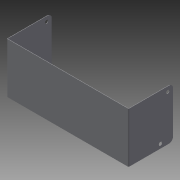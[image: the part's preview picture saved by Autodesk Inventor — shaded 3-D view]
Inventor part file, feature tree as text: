
AUTODESK INVENTOR PART (.ipt)
format: ipt  version: 2014 (Build 180170000, 170)  size: 122,368 bytes
history: native  units: mm
features: sheet_metal_op x4, sketch x3, other x2, chamfer x1, hole x1
ambient origin geometry x8: Origin, YZ Plane, XZ Plane, XY Plane, X Axis, Y Axis, Z Axis, Center Point
bodies: Solid1 (feature_tree)
feature tree (11):
  sheet_metal_op  "Face1"
  sheet_metal_op  "Flange1"
  chamfer  "Corner Round1"
  hole  "Hole1"  [1 undecoded]
  sketch  "Sketch1"  dims[d0=144.0mm d1=60.0mm]
  other  "Plate1"
  sketch  "Sketch3"  dims[d2=72.0mm]
  other  "Plate2"
  sheet_metal_op  "Bend1"
  sheet_metal_op  "Corner1"
  sketch  "Sketch4"  dims[d3=30.0mm d4=0.5mm d8=0.5mm d9=0.25mm d10=1.0mm d11=0.5mm d12=53.0mm d13=90.0deg d14=0.5mm d15=2.0mm d16=0.5mm d17=0.5mm d18=5.0mm d19=5.0mm d20=15.0mm d21=50.0mm d22=1.745329mm d23=4.0mm d24=6.0mm d25=4.0mm d26=2.0mm d27=90.0deg d28=0.5mm d29=20.594885mm]
note: 1 required parameter value undecoded (feature->parameter linkage not recoverable at this tier; creation-order binding heuristic only, values carry confidence <= 0.55)
